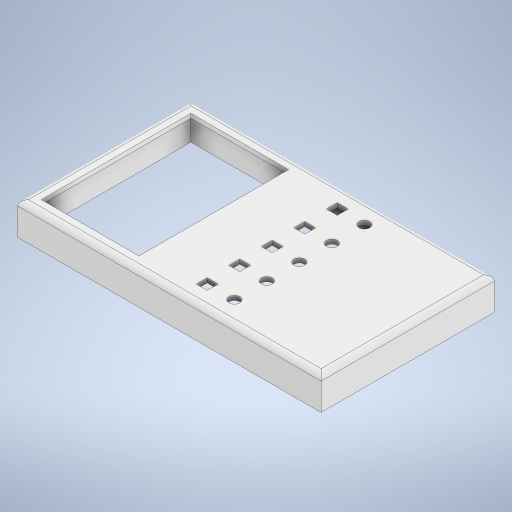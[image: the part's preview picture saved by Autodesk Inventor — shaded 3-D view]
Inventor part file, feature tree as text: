
AUTODESK INVENTOR PART (.ipt)
format: ipt  version: 2023 (Build 270158000, 158)  size: 314,368 bytes
history: native  units: in
note: dims shown in document units (in); Inventor stores cm internally (conversion verified against a paired STEP export)
features: extrude x2, sketch x2, fillet x1, shell x1
ambient origin geometry x8: Origin, YZ Plane, XZ Plane, XY Plane, X Axis, Y Axis, Z Axis, Center Point
bodies: Solid1 (feature_tree)
feature tree (6):
  extrude  "Extrusion1"  Depth=4.0in
  fillet  "Fillet1"  Radius=0.75in
  sketch  "Sketch2"  dims[d47=3.45in d48=2.25in d49=0.275in d50=0.275in d51=0.25in d52=0.25in d53=0.375in d54=3.0in d55=0.25in d56=0.25in d57=0.25in d58=0.25in d59=0.25in d60=0.25in d61=0.25in d62=0.25in d63=0.5in d64=0.5in d65=0.5in d66=0.5in d67=3.0in d68=0.25in d69=0.25in d70=0.25in d71=0.25in d72=0.25in d73=2.5in d74=2.5in d75=2.5in d76=2.5in d77=2.5in d78=0.5in d79=0.75in d80=0.75in d81=0.75in d82=0.75in d83=0.1in d84=0.75in d85=0.0in]
  shell  "Shell2"  Thickness=0.125in
  extrude  "Extrusion2"  Depth=2.25in
  sketch  "Sketch1"  dims[d0=7.0in d1=4.0in d43=0.75in d44=0.0in d45=0.125in]
